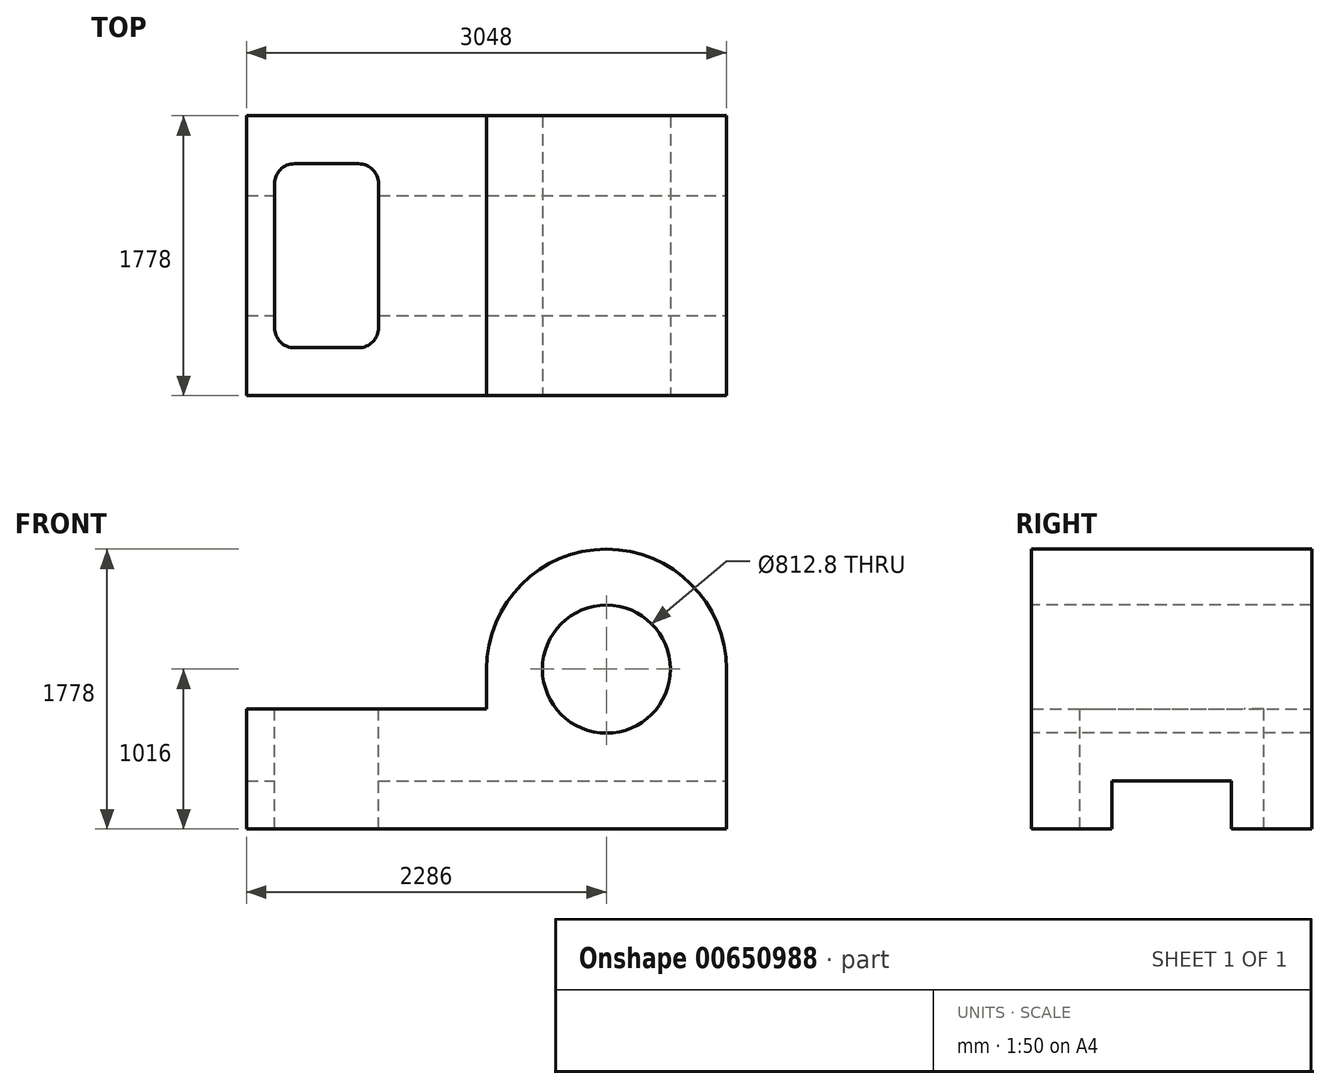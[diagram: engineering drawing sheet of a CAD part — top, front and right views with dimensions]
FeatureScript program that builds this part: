
annotation { "Feature Type Name" : "Feature", "Feature Type Description" : "" }
export const myFeature = defineFeature(function(context is Context, id is Id, definition is map)
    precondition{}
    {
        {
            var Q0;
            Q0=qCreatedBy(makeId("Front.planeOp"),FACE);
            var sketch = newSketch(context, id + "F0", { "sketchPlane" : qUnion([Q0])});
            skLineSegment(sketch, "E0.bottom", {"start": v(1524, -381) * mm, "end": v(-1524, -381) * mm});
            skLineSegment(sketch, "E0.left", {"start": v(1524, -381) * mm, "end": v(1524, 381) * mm});
            skLineSegment(sketch, "E0.right", {"start": v(-1524, -381) * mm, "end": v(-1524, 381) * mm});
            skPoint(sketch, "E0.middle", {"position": v(0, 0) * mm});
            skPoint(sketch, "E1.end.orphan", {"position": v(1524, 0) * mm});
            skPoint(sketch, "E1.start.orphan", {"position": v(762, 0) * mm});
            skLineSegment(sketch, "E2", {"start": v(-762, 381) * mm, "end": v(0, 381) * mm});
            skLineSegment(sketch, "E3.left", {"start": v(1524, 635) * mm, "end": v(1524, 127) * mm});
            skLineSegment(sketch, "E3.right", {"start": v(0, 635) * mm, "end": v(0, 381) * mm});
            skPoint(sketch, "E3.middle", {"position": v(762, 381) * mm});
            skPoint(sketch, "E4.orphan", {"position": v(0, 381) * mm});
            skLineSegment(sketch, "E5.trimOffspring", {"start": v(0, 381) * mm, "end": v(-1524, 381) * mm});
            skPoint(sketch, "E0.top.end.orphan", {"position": v(1143, 381) * mm});
            skPoint(sketch, "E6.orphan", {"position": v(0, 127) * mm});
            skArc(sketch, "E7", {"start": v(1524, 635) * mm, "mid": v(762, 1397) * mm, "end": v(0, 635) * mm});
            skSolve(sketch);
        }
        {
            var Q0;
            Q0=makeQuery(id+"F0.imprint","IMPRINT",FACE,{"disambiguationData":[TD([[makeQuery(id+"F0.imprint","IMPRINT",EDGE,{"derivedFrom":sQuery(id+"F0.wireOp",EDGE,"E0.bottom")}),-1.0]])]});
            extrude(context, id + "F1", {"entities" : qUnion([Q0]), "depth" : 1778 * mm, "offsetDistance" : 25.4 * mm});
        }
        {
            var Q0;
            Q0=makeQuery(id+"F1.opExtrude","CAP_FACE",FACE,{"disambiguationData":[OSD([sQuery(id+"F0.wireOp",EDGE,"E0.bottom"),sQuery(id+"F0.wireOp",EDGE,"E0.left"),sQuery(id+"F0.wireOp",EDGE,"E0.right"),sQuery(id+"F0.wireOp",EDGE,"E3.left"),sQuery(id+"F0.wireOp",EDGE,"E3.right"),sQuery(id+"F0.wireOp",EDGE,"E5.trimOffspring"),sQuery(id+"F0.wireOp",EDGE,"E7")])],"isStart":false});
            var sketch = newSketch(context, id + "F2", { "sketchPlane" : qUnion([Q0])});
            skCircle(sketch, "E8", {"center": v(762, 635) * mm, "radius": 406.4 * mm});
            skSolve(sketch);
        }
        {
            var Q0;
            Q0=makeQuery(id+"F2.imprint","IMPRINT",FACE,{"disambiguationData":[TD([[makeQuery(id+"F2.imprint","IMPRINT",EDGE,{"derivedFrom":sQuery(id+"F2.wireOp",EDGE,"E8")}),1.0]])]});
            extrude(context, id + "F3", {"entities" : qUnion([Q0]), "operationType" : NewBodyOperationType.REMOVE, "endBound" : BoundingType.THROUGH_ALL, "oppositeDirection" : true, "depth" : 25.4 * mm, "offsetDistance" : 25.4 * mm});
        }
        {
            var Q0;
            Q0=makeQuery(id+"F1.opExtrude","SWEPT_FACE",FACE,{"disambiguationData":[OSD([sQuery(id+"F0.wireOp",EDGE,"E0.left"),sQuery(id+"F0.wireOp",EDGE,"E3.left")])]});
            var sketch = newSketch(context, id + "F4", { "sketchPlane" : qUnion([Q0])});
            skLineSegment(sketch, "E9", {"start": v(-1778, -381) * mm, "end": v(0, -381) * mm});
            skLineSegment(sketch, "E10", {"start": v(0, -381) * mm, "end": v(-889, -381) * mm});
            skLineSegment(sketch, "E11.bottom", {"start": v(-508, -76.2) * mm, "end": v(-1270, -76.2) * mm});
            skLineSegment(sketch, "E11.left", {"start": v(-508, -76.2) * mm, "end": v(-508, -381) * mm});
            skLineSegment(sketch, "E11.right", {"start": v(-1270, -76.2) * mm, "end": v(-1270, -381) * mm});
            skPoint(sketch, "E11.middle", {"position": v(-889, -381) * mm});
            skPoint(sketch, "E12.orphan", {"position": v(-508, -685.8) * mm});
            skPoint(sketch, "E13.orphan", {"position": v(-1270, -685.8) * mm});
            skSolve(sketch);
        }
        {
            var Q0;
            Q0=makeQuery(id+"F4.imprint","IMPRINT",FACE,{"disambiguationData":[TD([[makeQuery(id+"F4.imprint","IMPRINT",EDGE,{"derivedFrom":sQuery(id+"F4.wireOp",EDGE,"E11.bottom")}),1.0]])]});
            extrude(context, id + "F5", {"entities" : qUnion([Q0]), "operationType" : NewBodyOperationType.REMOVE, "endBound" : BoundingType.THROUGH_ALL, "oppositeDirection" : true, "depth" : 25.4 * mm, "offsetDistance" : 25.4 * mm});
        }
        {
            var Q0;
            Q0=makeQuery(id+"F1.opExtrude","SWEPT_FACE",FACE,{"disambiguationData":[OSD([sQuery(id+"F0.wireOp",EDGE,"E5.trimOffspring")])]});
            var sketch = newSketch(context, id + "F6", { "sketchPlane" : qUnion([Q0])});
            skLineSegment(sketch, "E14", {"start": v(-1524, 0) * mm, "end": v(-1524, -889) * mm});
            skLineSegment(sketch, "E15.bottom", {"start": v(-812.8, -1473.2) * mm, "end": v(-1219.2, -1473.2) * mm});
            skLineSegment(sketch, "E15.top", {"start": v(-812.8, -304.8) * mm, "end": v(-1219.2, -304.8) * mm});
            skLineSegment(sketch, "E15.left", {"start": v(-685.8, -1346.2) * mm, "end": v(-685.8, -431.8) * mm});
            skLineSegment(sketch, "E15.right", {"start": v(-1346.2, -1346.2) * mm, "end": v(-1346.2, -431.8) * mm});
            skPoint(sketch, "E15.middle", {"position": v(-1016, -889) * mm});
            skPoint(sketch, "E16.visualSharp", {"position": v(-1346.2, -304.8) * mm});
            skArc(sketch, "E16.filletArc", {"start": v(-1219.2, -304.8) * mm, "mid": v(-1309, -342) * mm, "end": v(-1346.2, -431.8) * mm});
            skPoint(sketch, "E17.visualSharp", {"position": v(-685.8, -304.8) * mm});
            skArc(sketch, "E17.filletArc", {"start": v(-685.8, -431.8) * mm, "mid": v(-723, -342) * mm, "end": v(-812.8, -304.8) * mm});
            skPoint(sketch, "E18.visualSharp", {"position": v(-685.8, -1473.2) * mm});
            skArc(sketch, "E18.filletArc", {"start": v(-812.8, -1473.2) * mm, "mid": v(-723, -1436) * mm, "end": v(-685.8, -1346.2) * mm});
            skPoint(sketch, "E19.visualSharp", {"position": v(-1346.2, -1473.2) * mm});
            skArc(sketch, "E19.filletArc", {"start": v(-1346.2, -1346.2) * mm, "mid": v(-1309, -1436) * mm, "end": v(-1219.2, -1473.2) * mm});
            skSolve(sketch);
        }
        {
            var Q0;
            Q0=makeQuery(id+"F6.imprint","IMPRINT",FACE,{"disambiguationData":[TD([[makeQuery(id+"F6.imprint","IMPRINT",EDGE,{"derivedFrom":sQuery(id+"F6.wireOp",EDGE,"E15.bottom")}),-1.0]])]});
            extrude(context, id + "F7", {"entities" : qUnion([Q0]), "operationType" : NewBodyOperationType.REMOVE, "endBound" : BoundingType.THROUGH_ALL, "oppositeDirection" : true, "depth" : 25.4 * mm, "offsetDistance" : 25.4 * mm});
        }
    });
